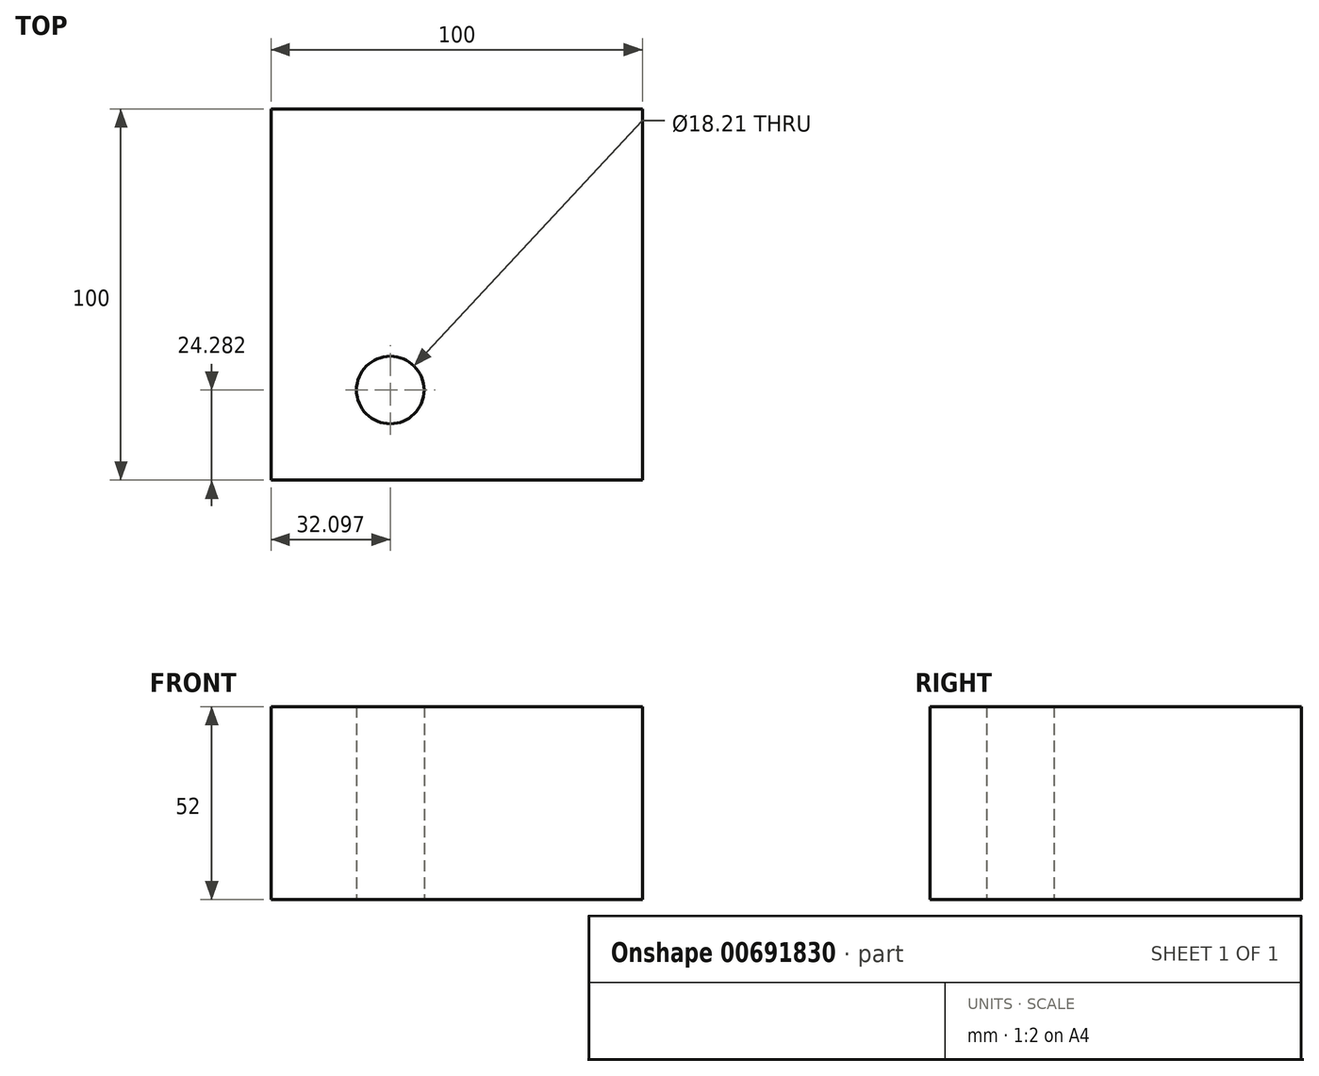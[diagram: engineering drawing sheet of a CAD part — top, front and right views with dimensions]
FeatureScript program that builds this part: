
annotation { "Feature Type Name" : "Feature", "Feature Type Description" : "" }
export const myFeature = defineFeature(function(context is Context, id is Id, definition is map)
    precondition{}
    {
        {
            var Q0;
            Q0=qCreatedBy(makeId("Top.planeOp"),FACE);
            var sketch = newSketch(context, id + "F0", { "sketchPlane" : qUnion([Q0])});
            skLineSegment(sketch, "E0.bottom", {"start": v(50, -50) * mm, "end": v(-50, -50) * mm});
            skLineSegment(sketch, "E0.top", {"start": v(50, 50) * mm, "end": v(-50, 50) * mm});
            skLineSegment(sketch, "E0.left", {"start": v(50, -50) * mm, "end": v(50, 50) * mm});
            skLineSegment(sketch, "E0.right", {"start": v(-50, -50) * mm, "end": v(-50, 50) * mm});
            skPoint(sketch, "E0.middle", {"position": v(0, 0) * mm});
            skCircle(sketch, "E1", {"center": v(-17.9, -25.72) * mm, "radius": 9.1 * mm});
            skSolve(sketch);
        }
        {
            var Q0;
            Q0 = qSketchRegion(id + "F0", true);
            extrude(context, id + "F1", {"entities" : qUnion([Q0]), "depth" : 52 * mm, "offsetDistance" : 25 * mm});
        }
    });
